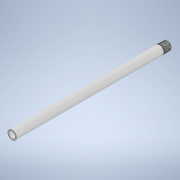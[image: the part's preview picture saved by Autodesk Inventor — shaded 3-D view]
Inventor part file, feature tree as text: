
AUTODESK INVENTOR PART (.ipt)
format: ipt  version: 2022 (Build 260153000, 153)  size: 804,352 bytes
history: native  units: in
note: dims shown in document units (in); Inventor stores cm internally (conversion verified against a paired STEP export)
features: extrude x1, sketch x1, revolve x1
ambient origin geometry x8: Origin, YZ Plane, XZ Plane, XY Plane, X Axis, Y Axis, Z Axis, Center Point
bodies: Solid1 (feature_tree)
feature tree (3):
  extrude  "Extrusion1"  [1 undecoded]
  sketch  "Sketch1"  dims[d0=15.0in d1=0.0in]
  revolve  "Revolve2"  [1 undecoded]
note: 2 required parameter values undecoded (feature->parameter linkage not recoverable at this tier; creation-order binding heuristic only, values carry confidence <= 0.55)
